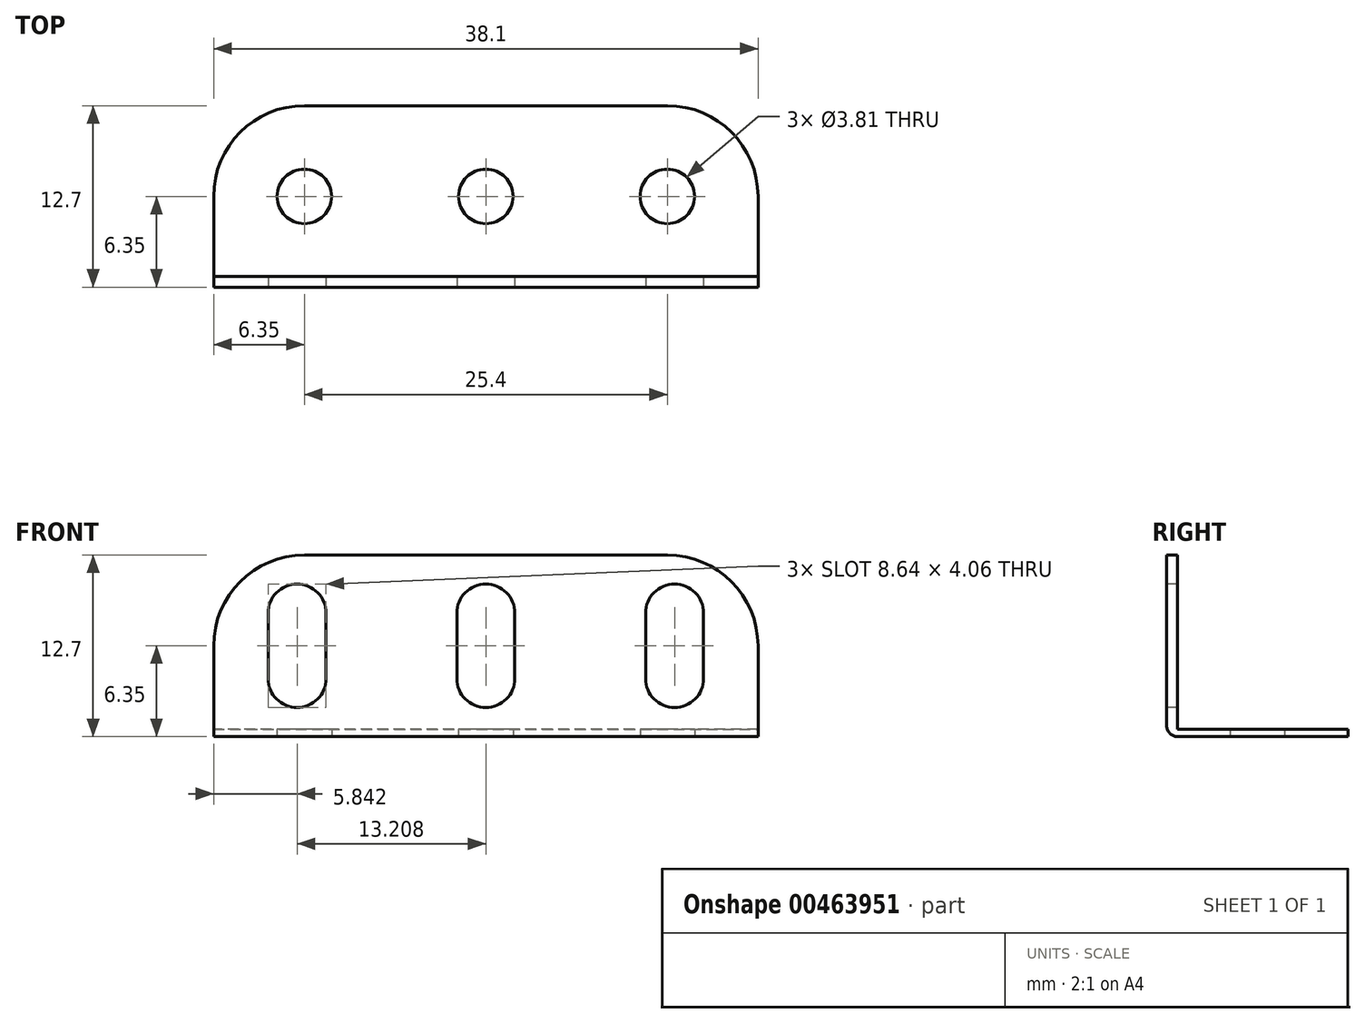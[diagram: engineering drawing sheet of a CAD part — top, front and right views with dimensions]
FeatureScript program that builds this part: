
annotation { "Feature Type Name" : "Feature", "Feature Type Description" : "" }
export const myFeature = defineFeature(function(context is Context, id is Id, definition is map)
    precondition{}
    {
        {
            var Q0;
            Q0=qCreatedBy(makeId("Top.planeOp"),FACE);
            var sketch = newSketch(context, id + "F0", { "sketchPlane" : qUnion([Q0])});
            skLineSegment(sketch, "E0.bottom", {"start": v(19.05, -6.35) * mm, "end": v(-19.05, -6.35) * mm});
            skLineSegment(sketch, "E0.top", {"start": v(12.7, 6.35) * mm, "end": v(-12.7, 6.35) * mm});
            skLineSegment(sketch, "E0.left", {"start": v(19.05, -6.35) * mm, "end": v(19.05, 0) * mm});
            skLineSegment(sketch, "E0.right", {"start": v(-19.05, -6.35) * mm, "end": v(-19.05, 0) * mm});
            skPoint(sketch, "E0.middle", {"position": v(0, 0) * mm});
            skPoint(sketch, "E1.visualSharp", {"position": v(-19.05, 6.35) * mm});
            skArc(sketch, "E1.filletArc", {"start": v(-12.7, 6.35) * mm, "mid": v(-17.2, 4.5) * mm, "end": v(-19.05, 0) * mm});
            skPoint(sketch, "E2.visualSharp", {"position": v(19.05, 6.35) * mm});
            skArc(sketch, "E2.filletArc", {"start": v(19.05, 0) * mm, "mid": v(17.2, 4.5) * mm, "end": v(12.7, 6.35) * mm});
            skSolve(sketch);
        }
        {
            var Q0;
            Q0=qCreatedBy(makeId("Top.planeOp"),FACE);
            var sketch = newSketch(context, id + "F1", { "sketchPlane" : qUnion([Q0])});
            skCircle(sketch, "E3", {"center": v(-12.7, 0) * mm, "radius": 1.9 * mm});
            skCircle(sketch, "E4", {"center": v(0, 0) * mm, "radius": 1.9 * mm});
            skCircle(sketch, "E5", {"center": v(12.7, 0) * mm, "radius": 1.9 * mm});
            skLineSegment(sketch, "E6.0", {"start": v(12.7, 6.35) * mm, "end": v(-12.7, 6.35) * mm});
            skArc(sketch, "E6.1", {"start": v(-12.7, 6.35) * mm, "mid": v(-17.2, 4.5) * mm, "end": v(-19.05, 0) * mm});
            skLineSegment(sketch, "E6.2", {"start": v(-19.05, -6.35) * mm, "end": v(-19.05, 0) * mm});
            skLineSegment(sketch, "E6.3", {"start": v(19.05, -6.35) * mm, "end": v(-19.05, -6.35) * mm});
            skLineSegment(sketch, "E6.4", {"start": v(19.05, -6.35) * mm, "end": v(19.05, 0) * mm});
            skArc(sketch, "E6.5", {"start": v(19.05, 0) * mm, "mid": v(17.2, 4.5) * mm, "end": v(12.7, 6.35) * mm});
            skSolve(sketch);
        }
        {
            var Q0;
            Q0=makeQuery(id+"F1.imprint","IMPRINT",FACE,{"disambiguationData":[TD([[makeQuery(id+"F1.imprint","IMPRINT",EDGE,{"derivedFrom":sQuery(id+"F1.wireOp",EDGE,"E3")}),-1.0]])]});
            extrude(context, id + "F2", {"entities" : qUnion([Q0]), "depth" : 0.5 * mm, "offsetDistance" : 25.4 * mm});
        }
        {
            var Q0;
            Q0=qCreatedBy(makeId("Front.planeOp"),FACE);
            var sketch = newSketch(context, id + "F3", { "sketchPlane" : qUnion([Q0])});
            skLineSegment(sketch, "E7.bottom", {"start": v(-19.05, 0) * mm, "end": v(19.05, 0) * mm});
            skLineSegment(sketch, "E7.top", {"start": v(-12.7, 12.7) * mm, "end": v(12.7, 12.7) * mm});
            skLineSegment(sketch, "E7.left", {"start": v(-19.05, 0) * mm, "end": v(-19.05, 6.35) * mm});
            skLineSegment(sketch, "E7.right", {"start": v(19.05, 0) * mm, "end": v(19.05, 6.35) * mm});
            skPoint(sketch, "E8.visualSharp", {"position": v(-19.05, 12.7) * mm});
            skArc(sketch, "E8.filletArc", {"start": v(-12.7, 12.7) * mm, "mid": v(-17.2, 10.84) * mm, "end": v(-19.05, 6.35) * mm});
            skPoint(sketch, "E9.visualSharp", {"position": v(19.05, 12.7) * mm});
            skArc(sketch, "E9.filletArc", {"start": v(19.05, 6.35) * mm, "mid": v(17.2, 10.84) * mm, "end": v(12.7, 12.7) * mm});
            skLineSegment(sketch, "E10.bottom", {"start": v(-15.24, 8.64) * mm, "end": v(-11.18, 8.64) * mm});
            skLineSegment(sketch, "E10.top", {"start": v(-15.24, 4.06) * mm, "end": v(-11.18, 4.06) * mm});
            skLineSegment(sketch, "E10.left", {"start": v(-15.24, 8.64) * mm, "end": v(-15.24, 4.06) * mm});
            skLineSegment(sketch, "E10.right", {"start": v(-11.18, 8.64) * mm, "end": v(-11.18, 4.06) * mm});
            skArc(sketch, "E11", {"start": v(-15.24, 8.64) * mm, "mid": v(-13.2, 10.67) * mm, "end": v(-11.18, 8.64) * mm});
            skArc(sketch, "E12", {"start": v(-11.18, 4.06) * mm, "mid": v(-13.2, 2.03) * mm, "end": v(-15.24, 4.06) * mm});
            skLineSegment(sketch, "E13", {"start": v(-19.05, 6.35) * mm, "end": v(19.05, 6.35) * mm, "construction": true});
            skArc(sketch, "E14.1.0.0", {"start": v(-2.03, 8.64) * mm, "mid": v(0, 10.67) * mm, "end": v(2.03, 8.64) * mm});
            skLineSegment(sketch, "E14.1.0.1", {"start": v(-2.03, 8.64) * mm, "end": v(2.03, 8.64) * mm});
            skLineSegment(sketch, "E14.1.0.2", {"start": v(-2.03, 8.64) * mm, "end": v(-2.03, 4.06) * mm});
            skLineSegment(sketch, "E14.1.0.3", {"start": v(-2.03, 4.06) * mm, "end": v(2.03, 4.06) * mm});
            skArc(sketch, "E14.1.0.4", {"start": v(2.03, 4.06) * mm, "mid": v(0, 2.03) * mm, "end": v(-2.03, 4.06) * mm});
            skLineSegment(sketch, "E14.1.0.5", {"start": v(2.03, 8.64) * mm, "end": v(2.03, 4.06) * mm});
            skArc(sketch, "E14.2.0.0", {"start": v(11.18, 8.64) * mm, "mid": v(13.2, 10.67) * mm, "end": v(15.24, 8.64) * mm});
            skLineSegment(sketch, "E14.2.0.1", {"start": v(11.18, 8.64) * mm, "end": v(15.24, 8.64) * mm});
            skLineSegment(sketch, "E14.2.0.2", {"start": v(11.18, 8.64) * mm, "end": v(11.18, 4.06) * mm});
            skLineSegment(sketch, "E14.2.0.3", {"start": v(11.18, 4.06) * mm, "end": v(15.24, 4.06) * mm});
            skArc(sketch, "E14.2.0.4", {"start": v(15.24, 4.06) * mm, "mid": v(13.2, 2.03) * mm, "end": v(11.18, 4.06) * mm});
            skLineSegment(sketch, "E14.2.0.5", {"start": v(15.24, 8.64) * mm, "end": v(15.24, 4.06) * mm});
            skLineSegment(sketch, "E14.direction1", {"start": v(-15.24, 8.64) * mm, "end": v(-2.03, 8.64) * mm, "construction": true});
            skSolve(sketch);
        }
        {
            var Q0;
            Q0=makeQuery(id+"F0.imprint","IMPRINT",FACE,{"disambiguationData":[TD([[makeQuery(id+"F0.imprint","IMPRINT",EDGE,{"derivedFrom":sQuery(id+"F0.wireOp",EDGE,"E0.bottom")}),-1.0]])]});
            var sketch = newSketch(context, id + "F4", { "sketchPlane" : qUnion([Q0])});
            skLineSegment(sketch, "E15.0", {"start": v(19.05, -6.35) * mm, "end": v(-19.05, -6.35) * mm});
            skLineSegment(sketch, "E15.1", {"start": v(-19.05, -6.35) * mm, "end": v(-19.05, -5.59) * mm});
            skLineSegment(sketch, "E15.2", {"start": v(19.05, -6.35) * mm, "end": v(19.05, -5.59) * mm});
            skLineSegment(sketch, "E16", {"start": v(-19.05, -5.59) * mm, "end": v(19.05, -5.59) * mm});
            skPoint(sketch, "E17.orphan", {"position": v(-19.05, 0) * mm});
            skPoint(sketch, "E18.orphan", {"position": v(19.05, 0) * mm});
            skSolve(sketch);
        }
        {
            var Q0;
            Q0=qCreatedBy(makeId("Front.planeOp"),FACE);
            cPlane(context, id + "F5", {"entities" : qUnion([Q0]), "cplaneType" : CPlaneType.OFFSET, "offset" : 6.35 * mm, "width" : 152.4 * mm, "height" : 152.4 * mm});
        }
        {
            var Q0;
            Q0=qCreatedBy(makeId("Front.planeOp"),FACE);
            var sketch = newSketch(context, id + "F6", { "sketchPlane" : qUnion([Q0])});
            skLineSegment(sketch, "E19.0", {"start": v(-19.05, 0) * mm, "end": v(-19.05, 6.35) * mm});
            skArc(sketch, "E19.1", {"start": v(-12.7, 12.7) * mm, "mid": v(-17.2, 10.84) * mm, "end": v(-19.05, 6.35) * mm});
            skLineSegment(sketch, "E19.2", {"start": v(-12.7, 12.7) * mm, "end": v(12.7, 12.7) * mm});
            skArc(sketch, "E19.3", {"start": v(19.05, 6.35) * mm, "mid": v(17.2, 10.84) * mm, "end": v(12.7, 12.7) * mm});
            skLineSegment(sketch, "E19.4", {"start": v(19.05, 0) * mm, "end": v(19.05, 6.35) * mm});
            skLineSegment(sketch, "E19.5", {"start": v(-19.05, 0) * mm, "end": v(19.05, 0) * mm});
            skArc(sketch, "E19.6", {"start": v(15.24, 4.06) * mm, "mid": v(13.2, 2.03) * mm, "end": v(11.18, 4.06) * mm});
            skLineSegment(sketch, "E19.7", {"start": v(15.24, 8.64) * mm, "end": v(15.24, 4.06) * mm});
            skArc(sketch, "E19.8", {"start": v(11.18, 8.64) * mm, "mid": v(13.2, 10.67) * mm, "end": v(15.24, 8.64) * mm});
            skLineSegment(sketch, "E19.9", {"start": v(11.18, 8.64) * mm, "end": v(11.18, 4.06) * mm});
            skArc(sketch, "E19.10", {"start": v(-2.03, 8.64) * mm, "mid": v(0, 10.67) * mm, "end": v(2.03, 8.64) * mm});
            skLineSegment(sketch, "E19.11", {"start": v(2.03, 8.64) * mm, "end": v(2.03, 4.06) * mm});
            skArc(sketch, "E19.12", {"start": v(2.03, 4.06) * mm, "mid": v(0, 2.03) * mm, "end": v(-2.03, 4.06) * mm});
            skLineSegment(sketch, "E19.13", {"start": v(-2.03, 8.64) * mm, "end": v(-2.03, 4.06) * mm});
            skArc(sketch, "E19.14", {"start": v(-11.18, 4.06) * mm, "mid": v(-13.2, 2.03) * mm, "end": v(-15.24, 4.06) * mm});
            skLineSegment(sketch, "E19.15", {"start": v(-11.18, 8.64) * mm, "end": v(-11.18, 4.06) * mm});
            skArc(sketch, "E19.16", {"start": v(-15.24, 8.64) * mm, "mid": v(-13.2, 10.67) * mm, "end": v(-11.18, 8.64) * mm});
            skLineSegment(sketch, "E19.17", {"start": v(-15.24, 8.64) * mm, "end": v(-15.24, 4.06) * mm});
            skPoint(sketch, "E19.18", {"position": v(15.24, 6.35) * mm});
            skSolve(sketch);
        }
        {
            var Q0;
            Q0=qCreatedBy(id+"F5.planeOp",FACE);
            var sketch = newSketch(context, id + "F7", { "sketchPlane" : qUnion([Q0])});
            skLineSegment(sketch, "E20.0", {"start": v(-19.05, 0) * mm, "end": v(-19.05, 6.35) * mm});
            skArc(sketch, "E20.1", {"start": v(-12.7, 12.7) * mm, "mid": v(-17.2, 10.84) * mm, "end": v(-19.05, 6.35) * mm});
            skLineSegment(sketch, "E20.2", {"start": v(-12.7, 12.7) * mm, "end": v(12.7, 12.7) * mm});
            skArc(sketch, "E20.3", {"start": v(19.05, 6.35) * mm, "mid": v(17.2, 10.84) * mm, "end": v(12.7, 12.7) * mm});
            skLineSegment(sketch, "E20.4", {"start": v(19.05, 0) * mm, "end": v(19.05, 6.35) * mm});
            skLineSegment(sketch, "E20.5", {"start": v(-19.05, 0) * mm, "end": v(19.05, 0) * mm});
            skArc(sketch, "E20.6", {"start": v(-11.18, 4.06) * mm, "mid": v(-13.2, 2.03) * mm, "end": v(-15.24, 4.06) * mm});
            skLineSegment(sketch, "E20.7", {"start": v(-15.24, 8.64) * mm, "end": v(-15.24, 4.06) * mm});
            skArc(sketch, "E20.8", {"start": v(-15.24, 8.64) * mm, "mid": v(-13.2, 10.67) * mm, "end": v(-11.18, 8.64) * mm});
            skLineSegment(sketch, "E20.9", {"start": v(-11.18, 8.64) * mm, "end": v(-11.18, 4.06) * mm});
            skLineSegment(sketch, "E20.10", {"start": v(-2.03, 8.64) * mm, "end": v(-2.03, 4.06) * mm});
            skArc(sketch, "E20.11", {"start": v(-2.03, 8.64) * mm, "mid": v(0, 10.67) * mm, "end": v(2.03, 8.64) * mm});
            skLineSegment(sketch, "E20.12", {"start": v(2.03, 8.64) * mm, "end": v(2.03, 4.06) * mm});
            skArc(sketch, "E20.13", {"start": v(2.03, 4.06) * mm, "mid": v(0, 2.03) * mm, "end": v(-2.03, 4.06) * mm});
            skArc(sketch, "E20.14", {"start": v(15.24, 4.06) * mm, "mid": v(13.2, 2.03) * mm, "end": v(11.18, 4.06) * mm});
            skLineSegment(sketch, "E20.15", {"start": v(15.24, 8.64) * mm, "end": v(15.24, 4.06) * mm});
            skArc(sketch, "E20.16", {"start": v(11.18, 8.64) * mm, "mid": v(13.2, 10.67) * mm, "end": v(15.24, 8.64) * mm});
            skLineSegment(sketch, "E20.17", {"start": v(11.18, 8.64) * mm, "end": v(11.18, 4.06) * mm});
            skSolve(sketch);
        }
        {
            var Q0;
            Q0 = qSketchRegion(id + "F7", true);
            extrude(context, id + "F8", {"entities" : qUnion([Q0]), "operationType" : NewBodyOperationType.ADD, "oppositeDirection" : true, "depth" : 0.76 * mm, "offsetDistance" : 25.4 * mm});
        }
        {
            var Q0;
            Q0=makeQuery(id+"F2.opExtrude","CAP_EDGE",EDGE,{"disambiguationData":[OSD([sQuery(id+"F1.wireOp",EDGE,"E6.3")])],"isStart":true});
            fillet(context, id + "F9", {"entities" : qUnion([Q0]), "radius" : 0.76 * mm, "tangentPropagation" : true, "allowEdgeOverflow" : false});
        }
    });
